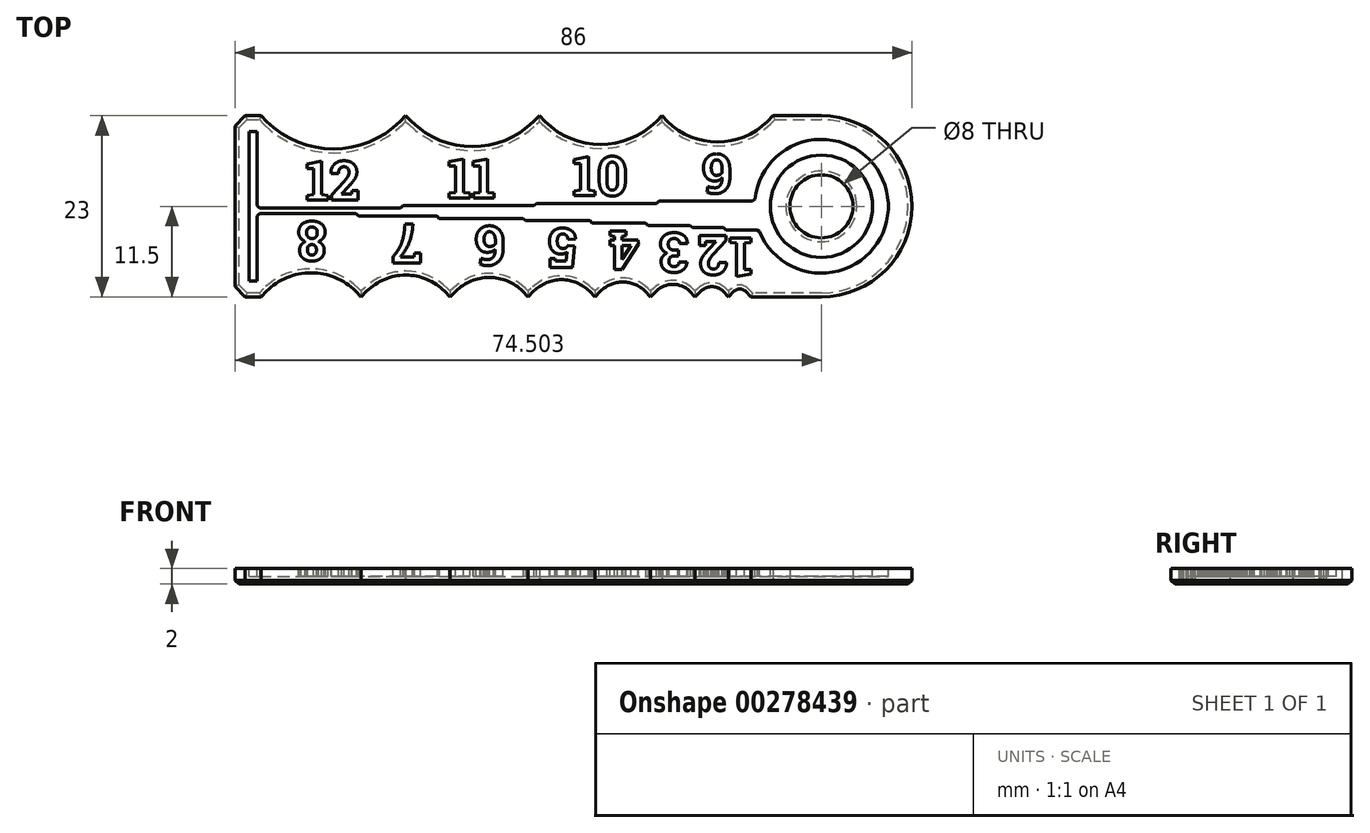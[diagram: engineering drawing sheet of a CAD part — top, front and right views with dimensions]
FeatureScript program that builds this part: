
annotation { "Feature Type Name" : "Feature", "Feature Type Description" : "" }
export const myFeature = defineFeature(function(context is Context, id is Id, definition is map)
    precondition{}
    {
        {
            var Q0;
            Q0=qCreatedBy(makeId("Top.planeOp"),FACE);
            var sketch = newSketch(context, id + "F0", { "sketchPlane" : qUnion([Q0])});
            skLineSegment(sketch, "E0.bottom", {"start": v(-50.91, 11.5) * mm, "end": v(50.91, 11.5) * mm, "construction": true});
            skLineSegment(sketch, "E0.top", {"start": v(-50.91, -11.5) * mm, "end": v(50.91, -11.5) * mm, "construction": true});
            skLineSegment(sketch, "E0.left", {"start": v(-50.91, 11.5) * mm, "end": v(-50.91, -11.5) * mm, "construction": true});
            skLineSegment(sketch, "E0.right", {"start": v(50.91, 11.5) * mm, "end": v(50.91, -11.5) * mm, "construction": true});
            skLineSegment(sketch, "E1", {"start": v(-50.91, 11.5) * mm, "end": v(-50.2, 10.8) * mm});
            skLineSegment(sketch, "E2", {"start": v(-33.23, 10.8) * mm, "end": v(-32.53, 11.5) * mm});
            skLineSegment(sketch, "E3", {"start": v(-32.53, 11.5) * mm, "end": v(-31.82, 10.8) * mm});
            skLineSegment(sketch, "E4", {"start": v(-16.26, 10.8) * mm, "end": v(-15.56, 11.5) * mm});
            skLineSegment(sketch, "E5", {"start": v(-15.56, 11.5) * mm, "end": v(-14.85, 10.8) * mm});
            skLineSegment(sketch, "E6", {"start": v(-0.7, 10.8) * mm, "end": v(0, 11.5) * mm});
            skLineSegment(sketch, "E7", {"start": v(0, 11.5) * mm, "end": v(0.7, 10.8) * mm});
            skLineSegment(sketch, "E8", {"start": v(13.44, 10.8) * mm, "end": v(14.14, 11.5) * mm});
            skPoint(sketch, "E9.visualSharp", {"position": v(-41.72, 2.3) * mm});
            skArc(sketch, "E9.filletArc", {"start": v(-50.2, 10.8) * mm, "mid": v(-41.72, 7.28) * mm, "end": v(-33.23, 10.8) * mm});
            skPoint(sketch, "E10.visualSharp", {"position": v(-24.04, 3.01) * mm});
            skArc(sketch, "E11.filletArc", {"start": v(-31.82, 10.8) * mm, "mid": v(-24.04, 7.57) * mm, "end": v(-16.26, 10.8) * mm});
            skPoint(sketch, "E12.visualSharp", {"position": v(-7.78, 3.72) * mm});
            skArc(sketch, "E12.filletArc", {"start": v(-14.85, 10.8) * mm, "mid": v(-7.78, 7.86) * mm, "end": v(-0.7, 10.8) * mm});
            skPoint(sketch, "E13.visualSharp", {"position": v(7.07, 4.43) * mm});
            skArc(sketch, "E13.filletArc", {"start": v(0.7, 10.8) * mm, "mid": v(7.07, 8.16) * mm, "end": v(13.44, 10.8) * mm});
            skLineSegment(sketch, "E14", {"start": v(-50.91, -11.5) * mm, "end": v(-50.2, -10.8) * mm});
            skLineSegment(sketch, "E15", {"start": v(-38.9, -10.8) * mm, "end": v(-38.18, -11.5) * mm});
            skLineSegment(sketch, "E16", {"start": v(-38.18, -11.5) * mm, "end": v(-37.48, -10.8) * mm});
            skLineSegment(sketch, "E17", {"start": v(-27.58, -10.8) * mm, "end": v(-26.87, -11.5) * mm});
            skLineSegment(sketch, "E18", {"start": v(-26.87, -11.5) * mm, "end": v(-26.16, -10.8) * mm});
            skLineSegment(sketch, "E19", {"start": v(-17.68, -10.8) * mm, "end": v(-16.97, -11.5) * mm});
            skLineSegment(sketch, "E20", {"start": v(-16.97, -11.5) * mm, "end": v(-16.26, -10.8) * mm});
            skLineSegment(sketch, "E21", {"start": v(-9.2, -10.8) * mm, "end": v(-8.49, -11.5) * mm});
            skPoint(sketch, "E22.visualSharp", {"position": v(-44.55, -5.14) * mm});
            skArc(sketch, "E22.filletArc", {"start": v(-38.9, -10.8) * mm, "mid": v(-44.55, -8.45) * mm, "end": v(-50.2, -10.8) * mm});
            skPoint(sketch, "E23.visualSharp", {"position": v(-32.53, -5.84) * mm});
            skArc(sketch, "E23.filletArc", {"start": v(-27.58, -10.8) * mm, "mid": v(-32.53, -8.74) * mm, "end": v(-37.48, -10.8) * mm});
            skPoint(sketch, "E24.visualSharp", {"position": v(-21.92, -6.55) * mm});
            skArc(sketch, "E24.filletArc", {"start": v(-17.68, -10.8) * mm, "mid": v(-21.92, -9.04) * mm, "end": v(-26.16, -10.8) * mm});
            skPoint(sketch, "E25.visualSharp", {"position": v(-12.73, -7.26) * mm});
            skArc(sketch, "E25.filletArc", {"start": v(-9.2, -10.8) * mm, "mid": v(-12.73, -9.33) * mm, "end": v(-16.26, -10.8) * mm});
            skLineSegment(sketch, "E26", {"start": v(-8.49, -11.5) * mm, "end": v(-7.78, -10.8) * mm});
            skLineSegment(sketch, "E27", {"start": v(-2.12, -10.8) * mm, "end": v(-1.41, -11.5) * mm});
            skLineSegment(sketch, "E28", {"start": v(-1.41, -11.5) * mm, "end": v(-0.7, -10.8) * mm});
            skLineSegment(sketch, "E29", {"start": v(3.54, -10.8) * mm, "end": v(4.24, -11.5) * mm});
            skLineSegment(sketch, "E30", {"start": v(4.24, -11.5) * mm, "end": v(4.95, -10.8) * mm});
            skLineSegment(sketch, "E31", {"start": v(7.78, -10.8) * mm, "end": v(8.49, -11.5) * mm});
            skLineSegment(sketch, "E32", {"start": v(8.49, -11.5) * mm, "end": v(9.2, -10.8) * mm});
            skLineSegment(sketch, "E33", {"start": v(10.6, -10.8) * mm, "end": v(11.31, -11.5) * mm});
            skPoint(sketch, "E34.visualSharp", {"position": v(-4.95, -7.96) * mm});
            skArc(sketch, "E34.filletArc", {"start": v(-2.12, -10.8) * mm, "mid": v(-4.95, -9.62) * mm, "end": v(-7.78, -10.8) * mm});
            skPoint(sketch, "E35.visualSharp", {"position": v(1.41, -8.67) * mm});
            skArc(sketch, "E35.filletArc", {"start": v(3.54, -10.8) * mm, "mid": v(1.41, -9.91) * mm, "end": v(-0.7, -10.8) * mm});
            skPoint(sketch, "E36.visualSharp", {"position": v(6.36, -9.38) * mm});
            skArc(sketch, "E36.filletArc", {"start": v(7.78, -10.8) * mm, "mid": v(6.36, -10.2) * mm, "end": v(4.95, -10.8) * mm});
            skPoint(sketch, "E37.visualSharp", {"position": v(9.9, -10.09) * mm});
            skArc(sketch, "E37.filletArc", {"start": v(10.6, -10.8) * mm, "mid": v(9.9, -10.5) * mm, "end": v(9.2, -10.8) * mm});
            skLineSegment(sketch, "E38", {"start": v(14.14, 11.5) * mm, "end": v(20.27, 11.5) * mm});
            skLineSegment(sketch, "E39", {"start": v(11.31, -11.5) * mm, "end": v(20.27, -11.5) * mm});
            skArc(sketch, "E40", {"start": v(20.27, -11.5) * mm, "mid": v(31.77, 0) * mm, "end": v(20.27, 11.5) * mm});
            skLineSegment(sketch, "E41", {"start": v(-50.91, 11.5) * mm, "end": v(-52.91, 11.5) * mm});
            skLineSegment(sketch, "E42", {"start": v(-54.23, -10.18) * mm, "end": v(-52.91, -11.5) * mm});
            skLineSegment(sketch, "E43", {"start": v(-54.23, 10.18) * mm, "end": v(-52.91, 11.5) * mm});
            skLineSegment(sketch, "E44", {"start": v(-54.23, 10.18) * mm, "end": v(-54.23, -10.18) * mm});
            skLineSegment(sketch, "E45", {"start": v(-52.91, -11.5) * mm, "end": v(-50.91, -11.5) * mm});
            skCircle(sketch, "E46", {"center": v(20.27, 0) * mm, "radius": 4 * mm});
            skSolve(sketch);
        }
        {
            var Q0;
            Q0 = qSketchRegion(id + "F0", true);
            extrude(context, id + "F1", {"entities" : qUnion([Q0]), "depth" : 2 * mm});
        }
        {
            var Q0;
            Q0=makeQuery(id+"F1.opExtrude","CAP_FACE",FACE,{"disambiguationData":[OSD([sQuery(id+"F0.wireOp",EDGE,"E1"),sQuery(id+"F0.wireOp",EDGE,"E2"),sQuery(id+"F0.wireOp",EDGE,"E3"),sQuery(id+"F0.wireOp",EDGE,"E4"),sQuery(id+"F0.wireOp",EDGE,"E5"),sQuery(id+"F0.wireOp",EDGE,"E6"),sQuery(id+"F0.wireOp",EDGE,"E7"),sQuery(id+"F0.wireOp",EDGE,"E8"),sQuery(id+"F0.wireOp",EDGE,"E9.filletArc"),sQuery(id+"F0.wireOp",EDGE,"E11.filletArc"),sQuery(id+"F0.wireOp",EDGE,"E12.filletArc"),sQuery(id+"F0.wireOp",EDGE,"E13.filletArc"),sQuery(id+"F0.wireOp",EDGE,"E14"),sQuery(id+"F0.wireOp",EDGE,"E15"),sQuery(id+"F0.wireOp",EDGE,"E16"),sQuery(id+"F0.wireOp",EDGE,"E17"),sQuery(id+"F0.wireOp",EDGE,"E18"),sQuery(id+"F0.wireOp",EDGE,"E19"),sQuery(id+"F0.wireOp",EDGE,"E20"),sQuery(id+"F0.wireOp",EDGE,"E21"),sQuery(id+"F0.wireOp",EDGE,"E22.filletArc"),sQuery(id+"F0.wireOp",EDGE,"E23.filletArc"),sQuery(id+"F0.wireOp",EDGE,"E24.filletArc"),sQuery(id+"F0.wireOp",EDGE,"E25.filletArc"),sQuery(id+"F0.wireOp",EDGE,"E26"),sQuery(id+"F0.wireOp",EDGE,"E27"),sQuery(id+"F0.wireOp",EDGE,"E28"),sQuery(id+"F0.wireOp",EDGE,"E29"),sQuery(id+"F0.wireOp",EDGE,"E30"),sQuery(id+"F0.wireOp",EDGE,"E31"),sQuery(id+"F0.wireOp",EDGE,"E32"),sQuery(id+"F0.wireOp",EDGE,"E33"),sQuery(id+"F0.wireOp",EDGE,"E34.filletArc"),sQuery(id+"F0.wireOp",EDGE,"E35.filletArc"),sQuery(id+"F0.wireOp",EDGE,"E36.filletArc"),sQuery(id+"F0.wireOp",EDGE,"E37.filletArc"),sQuery(id+"F0.wireOp",EDGE,"E38"),sQuery(id+"F0.wireOp",EDGE,"E39"),sQuery(id+"F0.wireOp",EDGE,"E40"),sQuery(id+"F0.wireOp",EDGE,"E41"),sQuery(id+"F0.wireOp",EDGE,"E42"),sQuery(id+"F0.wireOp",EDGE,"E43"),sQuery(id+"F0.wireOp",EDGE,"E44"),sQuery(id+"F0.wireOp",EDGE,"E45"),sQuery(id+"F0.wireOp",EDGE,"E46")])],"isStart":false});
            var sketch = newSketch(context, id + "F2", { "sketchPlane" : qUnion([Q0])});
            skText(sketch, "E47", { "text": "12", "fontName": "RobotoSlab-Bold.ttf"});
            skText(sketch, "E48", { "text": "11", "fontName": "RobotoSlab-Bold.ttf"});
            skText(sketch, "E49", { "text": "10", "fontName": "RobotoSlab-Bold.ttf"});
            skText(sketch, "E50", { "text": "9", "fontName": "RobotoSlab-Bold.ttf"});
            skLineSegment(sketch, "E51.bottom", {"start": v(-52.41, 9.5) * mm, "end": v(-51.41, 9.5) * mm});
            skLineSegment(sketch, "E51.top", {"start": v(-52.41, -9.5) * mm, "end": v(-51.41, -9.5) * mm});
            skLineSegment(sketch, "E51.left", {"start": v(-52.41, 9.5) * mm, "end": v(-52.41, -9.5) * mm});
            skLineSegment(sketch, "E51.right", {"start": v(-51.41, 9.5) * mm, "end": v(-51.41, -0.22) * mm});
            skCircle(sketch, "E52.0", {"center": v(20.27, 0) * mm, "radius": 6.5 * mm});
            skArc(sketch, "E53.0", {"start": v(12.32, -3) * mm, "mid": v(28.69, 1.2) * mm, "end": v(11.8, 0.66) * mm});
            skLineSegment(sketch, "E54", {"start": v(-51.91, 11.5) * mm, "end": v(-51.91, -11.5) * mm, "construction": true});
            skLineSegment(sketch, "E55", {"start": v(12.83, -0.8) * mm, "end": v(-51.91, -0.8) * mm, "construction": true});
            skLineSegment(sketch, "E56.trimOffspring", {"start": v(-51.41, -0.22) * mm, "end": v(-32.88, -0.22) * mm});
            skLineSegment(sketch, "E57.trimOffspring", {"start": v(-51.41, -0.95) * mm, "end": v(-51.41, -9.5) * mm});
            skLineSegment(sketch, "E58.trimOffspring", {"start": v(-51.41, -0.95) * mm, "end": v(-38.54, -0.95) * mm});
            skLineSegment(sketch, "E59", {"start": v(-28.26, -1.24) * mm, "end": v(-38.54, -1.24) * mm});
            skLineSegment(sketch, "E60", {"start": v(-32.88, 0.07) * mm, "end": v(-15.9, 0.07) * mm});
            skLineSegment(sketch, "E61", {"start": v(-15.9, 0.36) * mm, "end": v(-0.35, 0.36) * mm});
            skLineSegment(sketch, "E62", {"start": v(-17.32, -1.83) * mm, "end": v(-8.84, -1.83) * mm});
            skLineSegment(sketch, "E63", {"start": v(-8.84, -2.12) * mm, "end": v(-1.77, -2.12) * mm});
            skLineSegment(sketch, "E64", {"start": v(-1.77, -2.41) * mm, "end": v(3.89, -2.41) * mm});
            skLineSegment(sketch, "E65", {"start": v(3.89, -2.7) * mm, "end": v(8.13, -2.7) * mm});
            skLineSegment(sketch, "E66", {"start": v(8.13, -3) * mm, "end": v(12.32, -3) * mm});
            skLineSegment(sketch, "E67", {"start": v(-0.35, 0.66) * mm, "end": v(11.8, 0.66) * mm});
            skLineSegment(sketch, "E68", {"start": v(-32.88, -0.22) * mm, "end": v(-32.88, 0.07) * mm});
            skLineSegment(sketch, "E69", {"start": v(-38.54, -0.95) * mm, "end": v(-38.54, -1.24) * mm});
            skLineSegment(sketch, "E70", {"start": v(-28.26, -1.54) * mm, "end": v(-28.26, -1.24) * mm});
            skLineSegment(sketch, "E71", {"start": v(-15.9, 0.07) * mm, "end": v(-15.9, 0.36) * mm});
            skLineSegment(sketch, "E72", {"start": v(-8.84, -1.83) * mm, "end": v(-8.84, -2.12) * mm});
            skLineSegment(sketch, "E73", {"start": v(-1.77, -2.12) * mm, "end": v(-1.77, -2.41) * mm});
            skLineSegment(sketch, "E74", {"start": v(3.89, -2.41) * mm, "end": v(3.89, -2.7) * mm});
            skLineSegment(sketch, "E75", {"start": v(8.13, -2.7) * mm, "end": v(8.13, -3) * mm});
            skLineSegment(sketch, "E76", {"start": v(-0.35, 0.36) * mm, "end": v(-0.35, 0.66) * mm});
            skLineSegment(sketch, "E77", {"start": v(-28.26, -1.54) * mm, "end": v(-17.32, -1.54) * mm});
            skLineSegment(sketch, "E78", {"start": v(-17.32, -1.54) * mm, "end": v(-17.32, -1.83) * mm});
            skText(sketch, "E79", { "text": "8", "fontName": "RobotoSlab-Bold.ttf"});
            skText(sketch, "E80", { "text": "7", "fontName": "RobotoSlab-Bold.ttf"});
            skText(sketch, "E81", { "text": "6", "fontName": "RobotoSlab-Bold.ttf"});
            skText(sketch, "E82", { "text": "5", "fontName": "RobotoSlab-Bold.ttf"});
            skText(sketch, "E83", { "text": "4", "fontName": "RobotoSlab-Bold.ttf"});
            skText(sketch, "E84", { "text": "3", "fontName": "RobotoSlab-Bold.ttf"});
            skText(sketch, "E85", { "text": "2", "fontName": "RobotoSlab-Bold.ttf"});
            skText(sketch, "E86", { "text": "1", "fontName": "RobotoSlab-Bold.ttf"});
            const initialGuessF2  = {"E47": [-0.04528, 0.00078, 1, 0, 0.005], "E48": [-0.02723, 0.00107, 1, 0, 0.005], "E49": [-0.01136, 0.00136, 1, 0, 0.005], "E50": [0.00507, 0.00166, 1, 0, 0.005], "E79": [-0.04254, -0.00195, -1, 0, 0.005], "E80": [-0.03049, -0.00224, -1, 0, 0.005], "E81": [-0.01984, -0.00254, -1, 0, 0.005], "E82": [-0.01075, -0.00283, -1, 0, 0.005], "E83": [-0.00287, -0.00312, -1, 0, 0.005], "E84": [0.00343, -0.00341, -1, 0, 0.005], "E85": [0.00839, -0.00372, -1, 0, 0.005], "E86": [0.01155, -0.004, -1, 0, 0.005]};
            skSetInitialGuess(sketch, initialGuessF2);
            skSolve(sketch);
        }
        {
            var Q0;
            Q0 = qSketchRegion(id + "F2", true);
            extrude(context, id + "F3", {"entities" : qUnion([Q0]), "operationType" : NewBodyOperationType.REMOVE, "oppositeDirection" : true, "depth" : 1 * mm});
        }
        {
            var Q0;
            Q0=makeQuery(id+"F3.boolean.opBoolean","COPY",EDGE,{"derivedFrom":makeQuery(id+"F3.opExtrude","SWEPT_EDGE",EDGE,{"disambiguationData":[OSD([sQuery(id+"F2.wireOp",EDGE,"E60"),sQuery(id+"F2.wireOp",EDGE,"E71")])]})});
            var Q1;
            Q1=makeQuery(id+"F3.boolean.opBoolean","COPY",EDGE,{"derivedFrom":makeQuery(id+"F3.opExtrude","SWEPT_EDGE",EDGE,{"disambiguationData":[OSD([sQuery(id+"F2.wireOp",EDGE,"E61"),sQuery(id+"F2.wireOp",EDGE,"E76")])]})});
            var Q2;
            Q2=makeQuery(id+"F3.boolean.opBoolean","COPY",EDGE,{"derivedFrom":makeQuery(id+"F3.opExtrude","SWEPT_EDGE",EDGE,{"disambiguationData":[OSD([sQuery(id+"F2.wireOp",EDGE,"E53.0"),sQuery(id+"F2.wireOp",EDGE,"E67")])]})});
            var Q3;
            Q3=makeQuery(id+"F3.boolean.opBoolean","COPY",EDGE,{"derivedFrom":makeQuery(id+"F3.opExtrude","SWEPT_EDGE",EDGE,{"disambiguationData":[OSD([sQuery(id+"F2.wireOp",EDGE,"E56.trimOffspring"),sQuery(id+"F2.wireOp",EDGE,"E68")])]})});
            var Q4;
            Q4=makeQuery(id+"F3.boolean.opBoolean","COPY",EDGE,{"derivedFrom":makeQuery(id+"F3.opExtrude","SWEPT_EDGE",EDGE,{"disambiguationData":[OSD([sQuery(id+"F2.wireOp",EDGE,"E51.right"),sQuery(id+"F2.wireOp",EDGE,"E56.trimOffspring")])]})});
            var Q5;
            Q5=makeQuery(id+"F3.boolean.opBoolean","COPY",EDGE,{"derivedFrom":makeQuery(id+"F3.opExtrude","SWEPT_EDGE",EDGE,{"disambiguationData":[OSD([sQuery(id+"F2.wireOp",EDGE,"E57.trimOffspring"),sQuery(id+"F2.wireOp",EDGE,"E58.trimOffspring")])]})});
            var Q6;
            Q6=makeQuery(id+"F3.boolean.opBoolean","COPY",EDGE,{"derivedFrom":makeQuery(id+"F3.opExtrude","SWEPT_EDGE",EDGE,{"disambiguationData":[OSD([sQuery(id+"F2.wireOp",EDGE,"E65"),sQuery(id+"F2.wireOp",EDGE,"E75")])]})});
            var Q7;
            Q7=makeQuery(id+"F3.boolean.opBoolean","COPY",EDGE,{"derivedFrom":makeQuery(id+"F3.opExtrude","SWEPT_EDGE",EDGE,{"disambiguationData":[OSD([sQuery(id+"F2.wireOp",EDGE,"E64"),sQuery(id+"F2.wireOp",EDGE,"E74")])]})});
            var Q8;
            Q8=makeQuery(id+"F3.boolean.opBoolean","COPY",EDGE,{"derivedFrom":makeQuery(id+"F3.opExtrude","SWEPT_EDGE",EDGE,{"disambiguationData":[OSD([sQuery(id+"F2.wireOp",EDGE,"E63"),sQuery(id+"F2.wireOp",EDGE,"E73")])]})});
            var Q9;
            Q9=makeQuery(id+"F3.boolean.opBoolean","COPY",EDGE,{"derivedFrom":makeQuery(id+"F3.opExtrude","SWEPT_EDGE",EDGE,{"disambiguationData":[OSD([sQuery(id+"F2.wireOp",EDGE,"E62"),sQuery(id+"F2.wireOp",EDGE,"E72")])]})});
            var Q10;
            Q10=makeQuery(id+"F3.boolean.opBoolean","COPY",EDGE,{"derivedFrom":makeQuery(id+"F3.opExtrude","SWEPT_EDGE",EDGE,{"disambiguationData":[OSD([sQuery(id+"F2.wireOp",EDGE,"E77"),sQuery(id+"F2.wireOp",EDGE,"E78")])]})});
            var Q11;
            Q11=makeQuery(id+"F3.boolean.opBoolean","COPY",EDGE,{"derivedFrom":makeQuery(id+"F3.opExtrude","SWEPT_EDGE",EDGE,{"disambiguationData":[OSD([sQuery(id+"F2.wireOp",EDGE,"E59"),sQuery(id+"F2.wireOp",EDGE,"E70")])]})});
            var Q12;
            Q12=makeQuery(id+"F3.boolean.opBoolean","COPY",EDGE,{"derivedFrom":makeQuery(id+"F3.opExtrude","SWEPT_EDGE",EDGE,{"disambiguationData":[OSD([sQuery(id+"F2.wireOp",EDGE,"E58.trimOffspring"),sQuery(id+"F2.wireOp",EDGE,"E69")])]})});
            var Q13;
            Q13=makeQuery(id+"F3.boolean.opBoolean","COPY",EDGE,{"derivedFrom":makeQuery(id+"F3.opExtrude","SWEPT_EDGE",EDGE,{"disambiguationData":[OSD([sQuery(id+"F2.wireOp",EDGE,"E53.0"),sQuery(id+"F2.wireOp",EDGE,"E66")])]})});
            chamfer(context, id + "F4", {"entities" : qUnion([Q0, Q1, Q2, Q3, Q4, Q5, Q6, Q7, Q8, Q9, Q10, Q11, Q12, Q13]), "width" : .3 * mm, "tangentPropagation" : true});
        }
        {
            var Q0;
            Q0=makeQuery(id+"F1.opExtrude","CAP_FACE",FACE,{"disambiguationData":[OSD([sQuery(id+"F0.wireOp",EDGE,"E1"),sQuery(id+"F0.wireOp",EDGE,"E2"),sQuery(id+"F0.wireOp",EDGE,"E3"),sQuery(id+"F0.wireOp",EDGE,"E4"),sQuery(id+"F0.wireOp",EDGE,"E5"),sQuery(id+"F0.wireOp",EDGE,"E6"),sQuery(id+"F0.wireOp",EDGE,"E7"),sQuery(id+"F0.wireOp",EDGE,"E8"),sQuery(id+"F0.wireOp",EDGE,"E9.filletArc"),sQuery(id+"F0.wireOp",EDGE,"E11.filletArc"),sQuery(id+"F0.wireOp",EDGE,"E12.filletArc"),sQuery(id+"F0.wireOp",EDGE,"E13.filletArc"),sQuery(id+"F0.wireOp",EDGE,"E14"),sQuery(id+"F0.wireOp",EDGE,"E15"),sQuery(id+"F0.wireOp",EDGE,"E16"),sQuery(id+"F0.wireOp",EDGE,"E17"),sQuery(id+"F0.wireOp",EDGE,"E18"),sQuery(id+"F0.wireOp",EDGE,"E19"),sQuery(id+"F0.wireOp",EDGE,"E20"),sQuery(id+"F0.wireOp",EDGE,"E21"),sQuery(id+"F0.wireOp",EDGE,"E22.filletArc"),sQuery(id+"F0.wireOp",EDGE,"E23.filletArc"),sQuery(id+"F0.wireOp",EDGE,"E24.filletArc"),sQuery(id+"F0.wireOp",EDGE,"E25.filletArc"),sQuery(id+"F0.wireOp",EDGE,"E26"),sQuery(id+"F0.wireOp",EDGE,"E27"),sQuery(id+"F0.wireOp",EDGE,"E28"),sQuery(id+"F0.wireOp",EDGE,"E29"),sQuery(id+"F0.wireOp",EDGE,"E30"),sQuery(id+"F0.wireOp",EDGE,"E31"),sQuery(id+"F0.wireOp",EDGE,"E32"),sQuery(id+"F0.wireOp",EDGE,"E33"),sQuery(id+"F0.wireOp",EDGE,"E34.filletArc"),sQuery(id+"F0.wireOp",EDGE,"E35.filletArc"),sQuery(id+"F0.wireOp",EDGE,"E36.filletArc"),sQuery(id+"F0.wireOp",EDGE,"E37.filletArc"),sQuery(id+"F0.wireOp",EDGE,"E38"),sQuery(id+"F0.wireOp",EDGE,"E39"),sQuery(id+"F0.wireOp",EDGE,"E40"),sQuery(id+"F0.wireOp",EDGE,"E41"),sQuery(id+"F0.wireOp",EDGE,"E42"),sQuery(id+"F0.wireOp",EDGE,"E43"),sQuery(id+"F0.wireOp",EDGE,"E44"),sQuery(id+"F0.wireOp",EDGE,"E45"),sQuery(id+"F0.wireOp",EDGE,"E46")])],"isStart":true});
            chamfer(context, id + "F5", {"entities" : qUnion([Q0]), "width" : .5 * mm, "tangentPropagation" : true});
        }
    });
